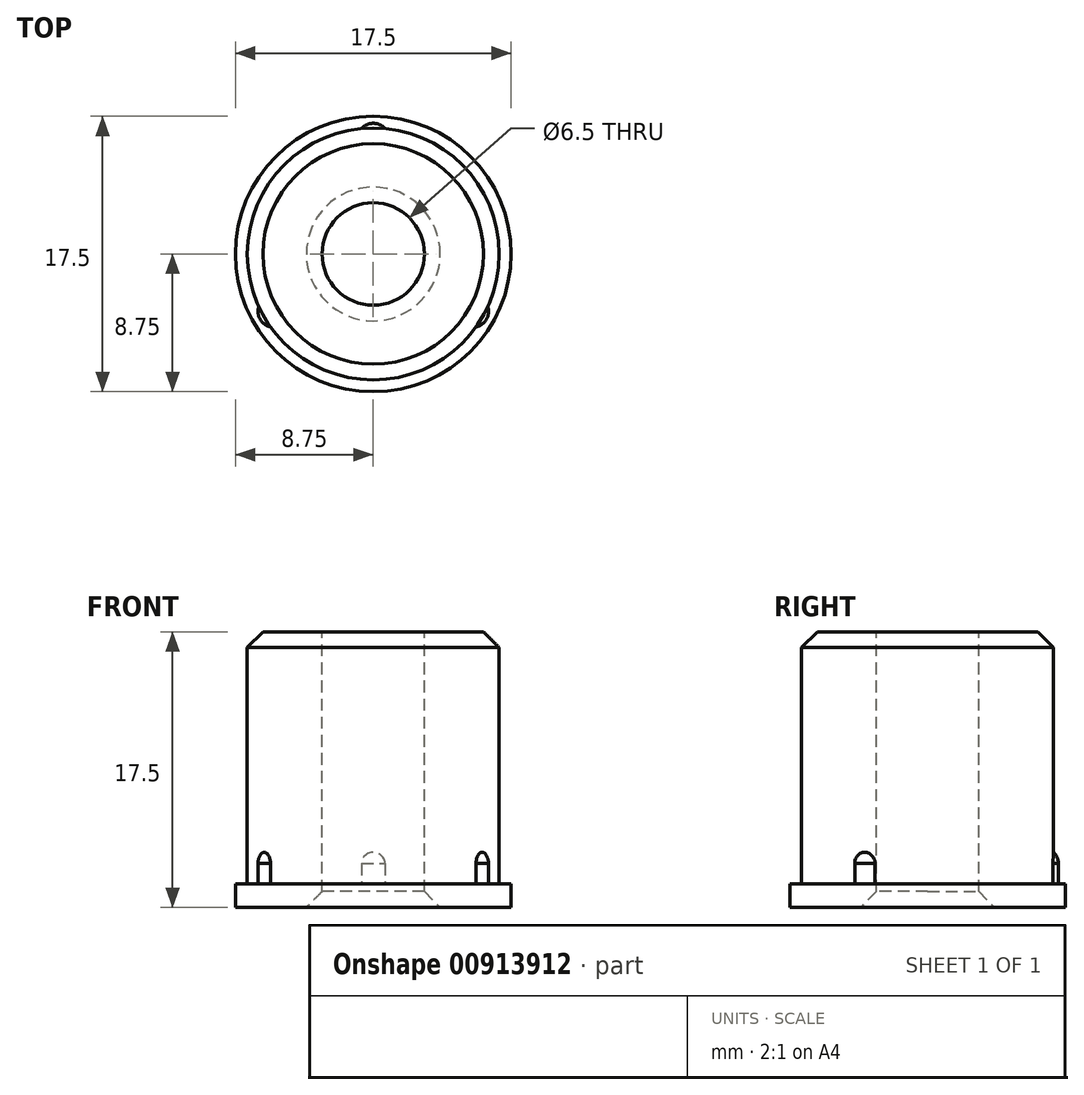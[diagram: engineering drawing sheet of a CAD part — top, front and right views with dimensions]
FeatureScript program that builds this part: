
annotation { "Feature Type Name" : "Feature", "Feature Type Description" : "" }
export const myFeature = defineFeature(function(context is Context, id is Id, definition is map)
    precondition{}
    {
        {
            var Q0;
            Q0=qCreatedBy(makeId("Front.planeOp"),FACE);
            var sketch = newSketch(context, id + "F0", { "sketchPlane" : qUnion([Q0])});
            skLineSegment(sketch, "E0", {"start": v(0, 30.84) * mm, "end": v(0, -22.07) * mm, "construction": true});
            skLineSegment(sketch, "E1", {"start": v(3.25, 0) * mm, "end": v(3.25, 17.5) * mm});
            skLineSegment(sketch, "E2", {"start": v(3.25, 17.5) * mm, "end": v(8, 17.5) * mm});
            skLineSegment(sketch, "E3", {"start": v(8, 17.5) * mm, "end": v(8, 1.5) * mm});
            skLineSegment(sketch, "E4", {"start": v(8, 1.5) * mm, "end": v(8.75, 1.5) * mm});
            skLineSegment(sketch, "E5", {"start": v(8.75, 1.5) * mm, "end": v(8.75, 0) * mm});
            skLineSegment(sketch, "E6", {"start": v(8.75, 0) * mm, "end": v(3.25, 0) * mm});
            skSolve(sketch);
        }
        {
            var Q0;
            Q0 = qSketchRegion(id + "F0", true);
            var Q1;
            Q1=sQuery(id+"F0.wireOp",EDGE,"E0");
            revolve(context, id + "F1", {"surfaceOperationType" : NewSurfaceOperationType.NEW, "entities" : qUnion([Q0]), "axis" : qUnion([Q1]), "revolveType" : RevolveType.FULL});
        }
        {
            var Q0;
            Q0=makeQuery(id+"F1.opRevolve","SWEPT_FACE",FACE,{"disambiguationData":[OSD([sQuery(id+"F0.wireOp",EDGE,"E4")])]});
            var sketch = newSketch(context, id + "F2", { "sketchPlane" : qUnion([Q0])});
            skArc(sketch, "E7.0", {"start": v(0.75, 7.97) * mm, "mid": v(0, 8) * mm, "end": v(-0.75, 7.97) * mm});
            skArc(sketch, "E8", {"start": v(0.75, 7.97) * mm, "mid": v(0, 8.3) * mm, "end": v(-0.75, 7.97) * mm});
            skArc(sketch, "E9.1.0", {"start": v(-7.27, -3.34) * mm, "mid": v(-7.19, -4.15) * mm, "end": v(-6.52, -4.63) * mm});
            skArc(sketch, "E9.1.1", {"start": v(-7.27, -3.34) * mm, "mid": v(-6.93, -4) * mm, "end": v(-6.52, -4.63) * mm});
            skArc(sketch, "E9.2.0", {"start": v(6.52, -4.63) * mm, "mid": v(7.19, -4.15) * mm, "end": v(7.27, -3.34) * mm});
            skArc(sketch, "E9.2.1", {"start": v(6.52, -4.63) * mm, "mid": v(6.93, -4) * mm, "end": v(7.27, -3.34) * mm});
            skSolve(sketch);
        }
        {
            var Q0;
            Q0 = qSketchRegion(id + "F2", true);
            extrude(context, id + "F3", {"entities" : qUnion([Q0]), "operationType" : NewBodyOperationType.ADD, "depth" : 2 * mm, "offsetDistance" : 25 * mm});
        }
        {
            var Q0;
            Q0=makeQuery(id+"F3.opExtrude","CAP_EDGE",EDGE,{"disambiguationData":[OSD([sQuery(id+"F2.wireOp",EDGE,"E9.2.0")])],"isStart":false});
            var Q1;
            Q1=makeQuery(id+"F3.opExtrude","CAP_EDGE",EDGE,{"disambiguationData":[OSD([sQuery(id+"F2.wireOp",EDGE,"E9.1.0")])],"isStart":false});
            var Q2;
            Q2=makeQuery(id+"F3.opExtrude","CAP_EDGE",EDGE,{"disambiguationData":[OSD([sQuery(id+"F2.wireOp",EDGE,"E8")])],"isStart":false});
            fillet(context, id + "F4", {"entities" : qUnion([Q0, Q1, Q2]), "radius" : 1 * mm, "tangentPropagation" : true, "allowEdgeOverflow" : false});
        }
        {
            var Q0;
            Q0=makeQuery(id+"F1.opRevolve","SWEPT_EDGE",EDGE,{"disambiguationData":[OSD([sQuery(id+"F0.wireOp",EDGE,"E2"),sQuery(id+"F0.wireOp",EDGE,"E3")])]});
            var Q1;
            Q1=makeQuery(id+"F1.opRevolve","SWEPT_EDGE",EDGE,{"disambiguationData":[OSD([sQuery(id+"F0.wireOp",EDGE,"E1"),sQuery(id+"F0.wireOp",EDGE,"E6")])]});
            chamfer(context, id + "F5", {"entities" : qUnion([Q0, Q1]), "width" : 1 * mm, "tangentPropagation" : true});
        }
    });
